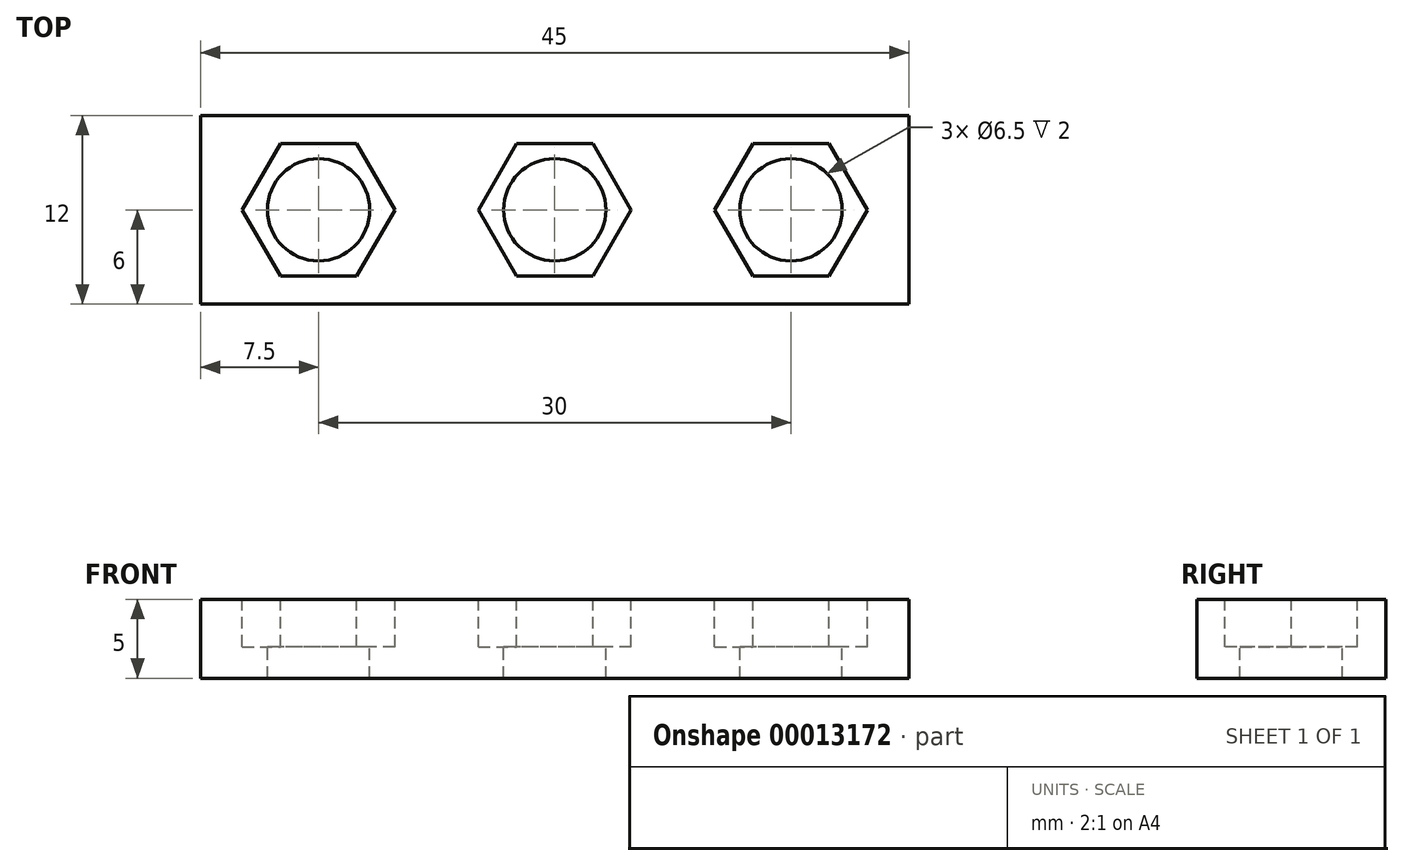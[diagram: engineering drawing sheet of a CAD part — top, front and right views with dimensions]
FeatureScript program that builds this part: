
annotation { "Feature Type Name" : "Feature", "Feature Type Description" : "" }
export const myFeature = defineFeature(function(context is Context, id is Id, definition is map)
    precondition{}
    {
        {
            var Q0;
            Q0=qCreatedBy(makeId("Top.planeOp"),FACE);
            var sketch = newSketch(context, id + "F0", { "sketchPlane" : qUnion([Q0])});
            skLineSegment(sketch, "E0.bottom", {"start": v(-22.5, 6) * mm, "end": v(22.5, 6) * mm});
            skLineSegment(sketch, "E0.top", {"start": v(-22.5, -6) * mm, "end": v(22.5, -6) * mm});
            skLineSegment(sketch, "E0.left", {"start": v(-22.5, 6) * mm, "end": v(-22.5, -6) * mm});
            skLineSegment(sketch, "E0.right", {"start": v(22.5, 6) * mm, "end": v(22.5, -6) * mm});
            skLineSegment(sketch, "E1", {"start": v(0, 0) * mm, "end": v(0, -6) * mm, "construction": true});
            skLineSegment(sketch, "E2", {"start": v(0, 0) * mm, "end": v(22.5, 0) * mm, "construction": true});
            skCircle(sketch, "E3.cCircle", {"center": v(0, 0) * mm, "radius": 4.2 * mm, "construction": true});
            skLineSegment(sketch, "E3.0", {"start": v(2.42, -4.2) * mm, "end": v(-2.42, -4.2) * mm});
            skLineSegment(sketch, "E3.1", {"start": v(-2.42, -4.2) * mm, "end": v(-4.85, 0) * mm});
            skLineSegment(sketch, "E3.2", {"start": v(-4.85, 0) * mm, "end": v(-2.42, 4.2) * mm});
            skLineSegment(sketch, "E3.3", {"start": v(-2.42, 4.2) * mm, "end": v(2.42, 4.2) * mm});
            skLineSegment(sketch, "E3.4", {"start": v(2.42, 4.2) * mm, "end": v(4.85, 0) * mm});
            skLineSegment(sketch, "E3.5", {"start": v(4.85, 0) * mm, "end": v(2.42, -4.2) * mm});
            skPoint(sketch, "E3.0.midPoint", {"position": v(0, -4.2) * mm});
            skCircle(sketch, "E4.cCircle", {"center": v(15, 0) * mm, "radius": 4.2 * mm, "construction": true});
            skLineSegment(sketch, "E4.0", {"start": v(17.42, -4.2) * mm, "end": v(12.58, -4.2) * mm});
            skLineSegment(sketch, "E4.1", {"start": v(12.58, -4.2) * mm, "end": v(10.15, 0) * mm});
            skLineSegment(sketch, "E4.2", {"start": v(10.15, 0) * mm, "end": v(12.58, 4.2) * mm});
            skLineSegment(sketch, "E4.3", {"start": v(12.58, 4.2) * mm, "end": v(17.42, 4.2) * mm});
            skLineSegment(sketch, "E4.4", {"start": v(17.42, 4.2) * mm, "end": v(19.85, 0) * mm});
            skLineSegment(sketch, "E4.5", {"start": v(19.85, 0) * mm, "end": v(17.42, -4.2) * mm});
            skPoint(sketch, "E4.0.midPoint", {"position": v(15, -4.2) * mm});
            skCircle(sketch, "E5.cCircle", {"center": v(-15, 0) * mm, "radius": 4.2 * mm, "construction": true});
            skLineSegment(sketch, "E5.0", {"start": v(-12.58, -4.2) * mm, "end": v(-17.42, -4.2) * mm});
            skLineSegment(sketch, "E5.1", {"start": v(-17.42, -4.2) * mm, "end": v(-19.85, 0) * mm});
            skLineSegment(sketch, "E5.2", {"start": v(-19.85, 0) * mm, "end": v(-17.42, 4.2) * mm});
            skLineSegment(sketch, "E5.3", {"start": v(-17.42, 4.2) * mm, "end": v(-12.58, 4.2) * mm});
            skLineSegment(sketch, "E5.4", {"start": v(-12.58, 4.2) * mm, "end": v(-10.15, 0) * mm});
            skLineSegment(sketch, "E5.5", {"start": v(-10.15, 0) * mm, "end": v(-12.58, -4.2) * mm});
            skPoint(sketch, "E5.0.midPoint", {"position": v(-15, -4.2) * mm});
            skLineSegment(sketch, "E6", {"start": v(-15, 0) * mm, "end": v(0, 0) * mm, "construction": true});
            skLineSegment(sketch, "E7", {"start": v(0, 0) * mm, "end": v(15, 0) * mm, "construction": true});
            skCircle(sketch, "E8", {"center": v(-15, 0) * mm, "radius": 3.25 * mm});
            skCircle(sketch, "E9", {"center": v(0, 0) * mm, "radius": 3.25 * mm});
            skCircle(sketch, "E10", {"center": v(15, 0) * mm, "radius": 3.25 * mm});
            skSolve(sketch);
        }
        {
            var Q0;
            Q0=makeQuery(id+"F0.imprint","IMPRINT",FACE,{"disambiguationData":[TD([[makeQuery(id+"F0.imprint","IMPRINT",EDGE,{"derivedFrom":sQuery(id+"F0.wireOp",EDGE,"E0.bottom")}),-1.0]])]});
            var Q1;
            Q1=makeQuery(id+"F0.imprint","IMPRINT",FACE,{"disambiguationData":[TD([[makeQuery(id+"F0.imprint","IMPRINT",EDGE,{"derivedFrom":sQuery(id+"F0.wireOp",EDGE,"E5.0")}),-1.0]])]});
            var Q2;
            Q2=makeQuery(id+"F0.imprint","IMPRINT",FACE,{"disambiguationData":[TD([[makeQuery(id+"F0.imprint","IMPRINT",EDGE,{"derivedFrom":sQuery(id+"F0.wireOp",EDGE,"E3.0")}),-1.0]])]});
            var Q3;
            Q3=makeQuery(id+"F0.imprint","IMPRINT",FACE,{"disambiguationData":[TD([[makeQuery(id+"F0.imprint","IMPRINT",EDGE,{"derivedFrom":sQuery(id+"F0.wireOp",EDGE,"E4.0")}),-1.0]])]});
            extrude(context, id + "F1", {"entities" : qUnion([Q0, Q1, Q2, Q3]), "oppositeDirection" : true, "depth" : 5 * mm});
        }
        {
            var Q0;
            Q0=makeQuery(id+"F0.imprint","IMPRINT",FACE,{"disambiguationData":[TD([[makeQuery(id+"F0.imprint","IMPRINT",EDGE,{"derivedFrom":sQuery(id+"F0.wireOp",EDGE,"E5.0")}),-1.0]])]});
            var Q1;
            Q1=makeQuery(id+"F0.imprint","IMPRINT",FACE,{"disambiguationData":[TD([[makeQuery(id+"F0.imprint","IMPRINT",EDGE,{"derivedFrom":sQuery(id+"F0.wireOp",EDGE,"E3.0")}),-1.0]])]});
            var Q2;
            Q2=makeQuery(id+"F0.imprint","IMPRINT",FACE,{"disambiguationData":[TD([[makeQuery(id+"F0.imprint","IMPRINT",EDGE,{"derivedFrom":sQuery(id+"F0.wireOp",EDGE,"E4.0")}),-1.0]])]});
            var Q3;
            Q3=makeQuery(id+"F1.opExtrude","CAP_FACE",FACE,{"disambiguationData":[OSD([sQuery(id+"F0.wireOp",EDGE,"E0.bottom"),sQuery(id+"F0.wireOp",EDGE,"E0.top"),sQuery(id+"F0.wireOp",EDGE,"E0.left"),sQuery(id+"F0.wireOp",EDGE,"E0.right"),sQuery(id+"F0.wireOp",EDGE,"E8"),sQuery(id+"F0.wireOp",EDGE,"E9"),sQuery(id+"F0.wireOp",EDGE,"E10")])],"isStart":false});
            extrude(context, id + "F2", {"entities" : qUnion([Q0, Q1, Q2]), "operationType" : NewBodyOperationType.REMOVE, "oppositeDirection" : true, "endBoundEntity" : qUnion([Q3]), "depth" : 3 * mm});
        }
    });
